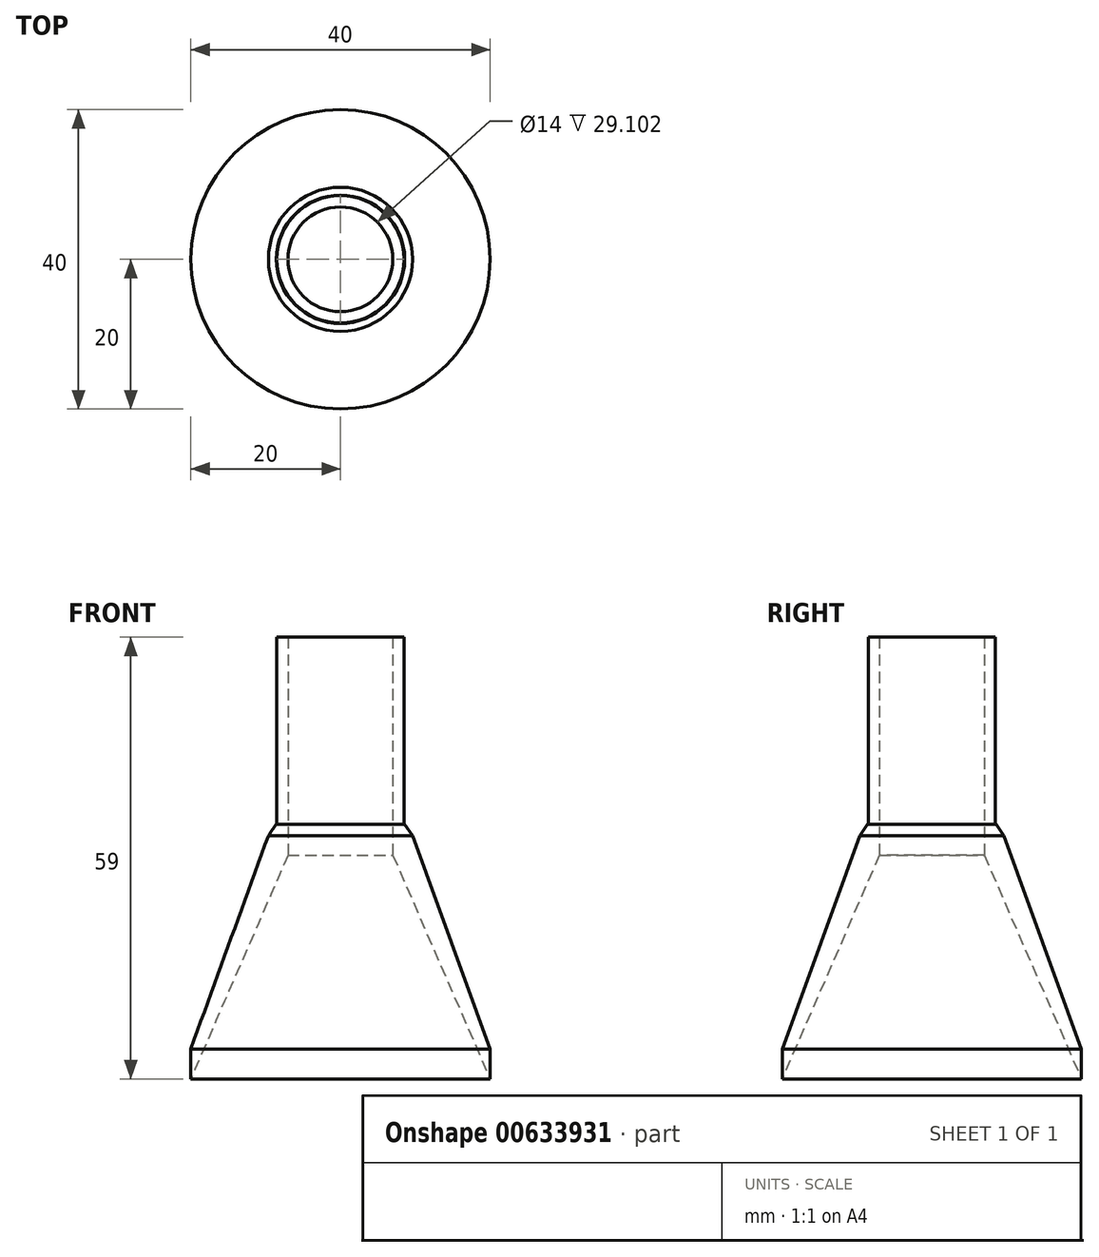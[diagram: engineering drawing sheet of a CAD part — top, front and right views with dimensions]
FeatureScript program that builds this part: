
annotation { "Feature Type Name" : "Feature", "Feature Type Description" : "" }
export const myFeature = defineFeature(function(context is Context, id is Id, definition is map)
    precondition{}
    {
        {
            var Q0;
            Q0=qCreatedBy(makeId("Top.planeOp"),FACE);
            var sketch = newSketch(context, id + "F0", { "sketchPlane" : qUnion([Q0])});
            skCircle(sketch, "E0", {"center": v(0, 0) * mm, "radius": 7 * mm});
            skCircle(sketch, "E1", {"center": v(0, 0) * mm, "radius": 8.5 * mm});
            skSolve(sketch);
        }
        {
            var Q0;
            Q0 = qSketchRegion(id + "F0", true);
            extrude(context, id + "F1", {"entities" : qUnion([Q0]), "depth" : 25 * mm, "offsetDistance" : 25 * mm});
        }
        {
            var Q0;
            Q0=makeQuery(id+"F1.opExtrude","CAP_FACE",FACE,{"disambiguationData":[OSD([sQuery(id+"F0.wireOp",EDGE,"E0"),sQuery(id+"F0.wireOp",EDGE,"E1")])],"isStart":true});
            var sketch = newSketch(context, id + "F2", { "sketchPlane" : qUnion([Q0])});
            skCircle(sketch, "E2", {"center": v(0, 0) * mm, "radius": 20 * mm});
            skSolve(sketch);
        }
        {
            var Q0;
            Q0 = qSketchRegion(id + "F2", true);
            extrude(context, id + "F3", {"entities" : qUnion([Q0]), "operationType" : NewBodyOperationType.ADD, "depth" : 34 * mm, "offsetDistance" : 25 * mm});
        }
        {
            var Q0;
            Q0=makeQuery(id+"F3.opExtrude","CAP_FACE",FACE,{"disambiguationData":[OSD([sQuery(id+"F2.wireOp",EDGE,"E2")])],"isStart":false});
            var sketch = newSketch(context, id + "F4", { "sketchPlane" : qUnion([Q0])});
            skLineSegment(sketch, "E3", {"start": v(0, 0) * mm, "end": v(-20, 0) * mm, "construction": true});
            skLineSegment(sketch, "E4", {"start": v(0, 0) * mm, "end": v(20, 0) * mm, "construction": true});
            skLineSegment(sketch, "E5", {"start": v(0, 0) * mm, "end": v(0, 20) * mm, "construction": true});
            skLineSegment(sketch, "E6", {"start": v(0, 0) * mm, "end": v(0, -20) * mm, "construction": true});
            skSolve(sketch);
        }
        {
            var Q0;
            Q0=sQuery(id+"F4.wireOp",VERTEX,"E6.start");
            var Q1;
            Q1=makeQuery(id+"F1.opExtrude","SWEPT_BODY",BODY,{"disambiguationData":[OSD([sQuery(id+"F0.wireOp",EDGE,"E0"),sQuery(id+"F0.wireOp",EDGE,"E1")])]});
            hole(context, id + "F5", {"style" : HoleStyle.C_SINK, "endStyle" : HoleEndStyle.THROUGH, "holeDiameter" : 14 * mm, "cSinkDiameter" : 40 * mm, "cSinkAngle" : 47 * degree, "majorDiameter" : 5 * mm, "isTappedThrough" : true, "tappedDepth" : 12 * mm, "tapClearance" : 3, "locations" : qUnion([Q0]), "scope" : qUnion([Q1])});
        }
        {
            var Q0;
            Q0=makeQuery(id+"F3.opExtrude","CAP_EDGE",EDGE,{"disambiguationData":[OSD([sQuery(id+"F2.wireOp",EDGE,"E2")])],"isStart":true});
            chamfer(context, id + "F6", {"entities" : qUnion([Q0]), "chamferType" : ChamferType.OFFSET_ANGLE, "width" : 30 * mm, "oppositeDirection" : false, "angle" : 20 * degree, "tangentPropagation" : true});
        }
        {
            var Q0;
            {var subQ0=sQuery(id+"F2.wireOp",EDGE,"E2");Q0=makeQuery(id+"F6.opChamfer","BLEND_EDGE",EDGE,{"blendedFrom":[makeQuery(id+"F3.opExtrude","CAP_EDGE",EDGE,{"disambiguationData":[OSD([subQ0])],"isStart":true}),makeQuery(id+"F3.boolean.opBoolean","SPLIT",FACE,{"disambiguationData":[TD([makeQuery(id+"F1.opExtrude","SWEPT_FACE",FACE,{"disambiguationData":[OSD([sQuery(id+"F0.wireOp",EDGE,"E1")])]})])],"derivedFrom":makeQuery(id+"F3.opExtrude","CAP_FACE",FACE,{"disambiguationData":[OSD([subQ0])],"isStart":true})})],"blendedInto":[makeQuery(id+"F3.boolean.opBoolean","SPLIT",FACE,{"disambiguationData":[TD([makeQuery(id+"F1.opExtrude","SWEPT_FACE",FACE,{"disambiguationData":[OSD([sQuery(id+"F0.wireOp",EDGE,"E1")])]})])],"derivedFrom":makeQuery(id+"F3.opExtrude","CAP_FACE",FACE,{"disambiguationData":[OSD([subQ0])],"isStart":true})})]});}
            chamfer(context, id + "F7", {"entities" : qUnion([Q0]), "chamferType" : ChamferType.OFFSET_ANGLE, "width" : .5 * mm, "oppositeDirection" : false, "angle" : 55 * degree, "tangentPropagation" : true});
        }
    });
